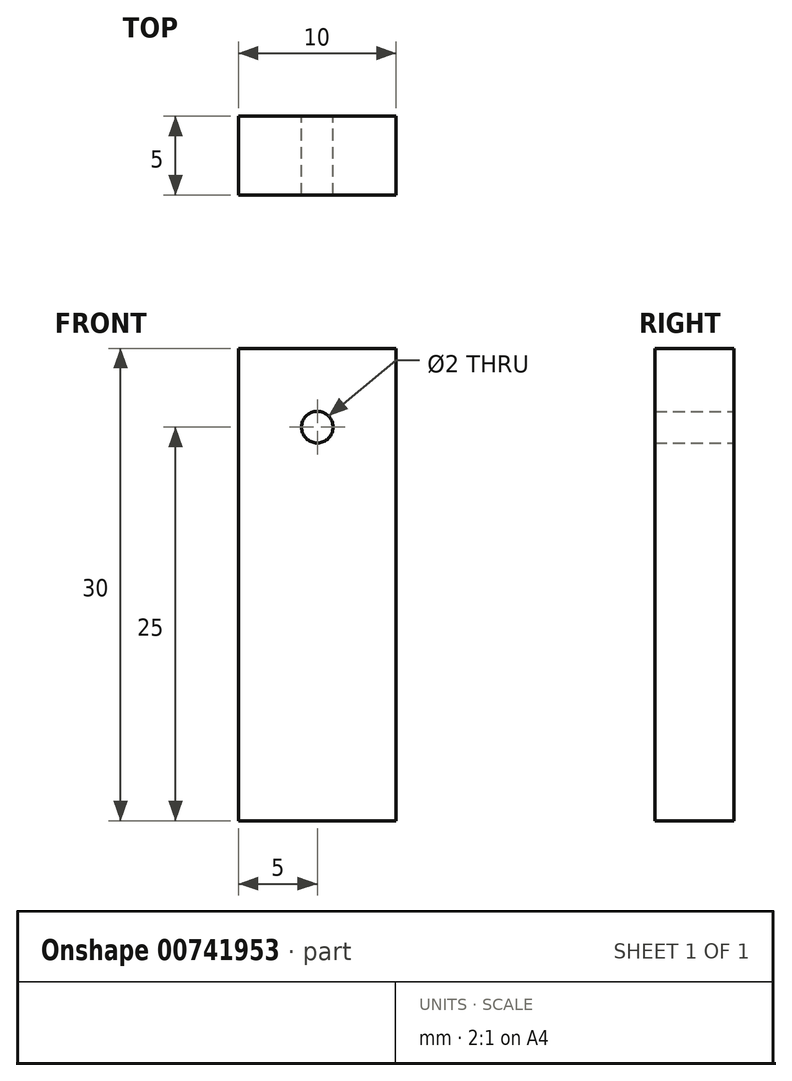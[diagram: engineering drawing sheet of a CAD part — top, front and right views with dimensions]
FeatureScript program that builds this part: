
annotation { "Feature Type Name" : "Feature", "Feature Type Description" : "" }
export const myFeature = defineFeature(function(context is Context, id is Id, definition is map)
    precondition{}
    {
        {
            var Q0;
            Q0=qCreatedBy(makeId("Front.planeOp"),FACE);
            var sketch = newSketch(context, id + "F0", { "sketchPlane" : qUnion([Q0])});
            skLineSegment(sketch, "E0.bottom", {"start": v(5, -15) * mm, "end": v(-5, -15) * mm});
            skLineSegment(sketch, "E0.top", {"start": v(5, 15) * mm, "end": v(-5, 15) * mm});
            skLineSegment(sketch, "E0.left", {"start": v(5, -15) * mm, "end": v(5, 15) * mm});
            skLineSegment(sketch, "E0.right", {"start": v(-5, -15) * mm, "end": v(-5, 15) * mm});
            skPoint(sketch, "E0.middle", {"position": v(0, 0) * mm});
            skSolve(sketch);
        }
        {
            var Q0;
            Q0 = qSketchRegion(id + "F0", true);
            extrude(context, id + "F1", {"entities" : qUnion([Q0]), "depth" : 5 * mm, "offsetDistance" : 25 * mm});
        }
        {
            var Q0;
            Q0=qCreatedBy(makeId("Front.planeOp"),FACE);
            var sketch = newSketch(context, id + "F2", { "sketchPlane" : qUnion([Q0])});
            skCircle(sketch, "E1", {"center": v(0, 10) * mm, "radius": 1 * mm});
            skSolve(sketch);
        }
        {
            var Q0;
            Q0 = qSketchRegion(id + "F2", true);
            extrude(context, id + "F3", {"entities" : qUnion([Q0]), "operationType" : NewBodyOperationType.REMOVE, "depth" : 10 * mm, "offsetDistance" : 25 * mm});
        }
    });
